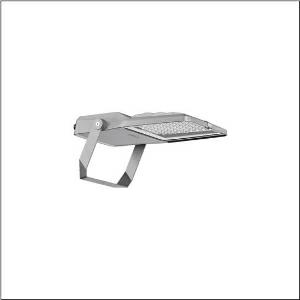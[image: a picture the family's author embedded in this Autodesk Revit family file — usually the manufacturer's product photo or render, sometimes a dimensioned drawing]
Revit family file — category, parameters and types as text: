
# Revit family: floodlight_fl_21_iq_mini___pl52_5xa7771c4d1a_1f8c
name_source: partatom
category: Lighting Fixtures
units: mm (PartAtom-declared; Revit-internal decimal feet)

## family parameters
Cut with Voids When Loaded = No
Host = Face
Light Source = No
Part Type = Normal
Room Calculation Point = No
Round Connector Dimension = Use Diameter
Shared = No

## types (1)
- --- (1 x LED, 12720 lm, 87.2 W, 4000K)
    Apparent Load = 87 VA
    CIE Flux Codes = 26 60 98 100 100
    Color Rendering = 70
    Color Temperature = 4000K
    Default Elevation = 1800 mm
    Description = Floodlight FL 21 iQ mini, floodlight, primary light control with lens, of PMMA, primary optical cover: protective disc, of toughened safety glass, transparent, light distribution: PL52, light emission: direct distribution, installation type: surface-mounted, LED, High Power LED, rated luminous flux: 12.720lm, luminous efficacy: 146lm/W, light colour: 740, colour temperature: 4000K, control gear: iQ Comfort/DALI, control: Auto-Match, Temp-Guard, Lumen-Switch, Night-Set, Smart-Wire, Light-Fading, Desk-Remote (wireless, voltage-free reading and setting of iQ features in the workshop via application-optimized NFC function/RFID function), optimised constant luminous flux control (CLO 2.0), with terminal, 6-pole, mains connection: 220..240V, AC, 50/60Hz, start of lifetime: 87W, end of service life: 92W, reduction: 40W, luminaire housing, of diecast aluminium, powder-coated, Siteco® metallic grey (DB 702S), corrosivity category C5 mid according to DIN EN ISO 12944, suitable for swimming pools, chlorine-resistant, sealing non-destructively replaceable, mounting bracket, of steel, galvanised, powder-coated, Siteco® metallic grey (DB 702S), protection rating (complete): IP66, insulation class (complete): insulation class II (safety insulation), certification: CE, ENEC, VDE, protection symbol: D, impact resistance: IK08, permissible operating ambient temperature: -40..+40°C, permissible operating ambient temperature for outdoor applications: -40..+50°C, standard: DIN EN 12944, LABS conformity tested according to VDMA 24364:2018-05, packaging unit: 1 piece

Light Distribution: PL52
    Height = 70 mm
    Lamp = 1 x LED
    Lamp Light Flux = 12720 lm
    Lamp Power = 87.2 W
    Lamp count = 1
    Length = 485 mm
    Luminous efficacy = 146 lm/W
    Manufacturer = Siteco
    ModVariant = No
    Model = 5XA7771C4D1A
    Number of Poles = 1
    OnlyDefault = Yes
    Power Factor = 1
    Product Name = Floodlight FL 21 iQ mini | PL52
    Product group = floodlight | pylon annexe
    ProductGroupID = 6200
    Protection Class = Protection class II
    Protection Degree = IP 66
    RLX_Detail_Level = 1
    RLX_Emergency_Light_Flux = 0 lm
    RLX_Emergency_Type = 0
    RLX_Emergency_Type_DB = No
    RlxData = <blob elided: 96621 chars, md5=81f84f79>
    Socket = socket
    Standby Power = 0 W
    System Light Flux = 12720 lm
    System Power = 87 W
    Type Comments = factory setting: luminous flux: 100 % | dim-lin: 254 | 456 mA
    Type Image = l_1006845.jpg
    URL = http://relux.com
    VarID = @adj_164520
    Voltage = 0 V
    Weight = 0.00 kg
    Width = 337 mm

## geometry (parser evidence)
native form markers: Blend x4, Sweep x11
no freeform markers — native parametric forms only
